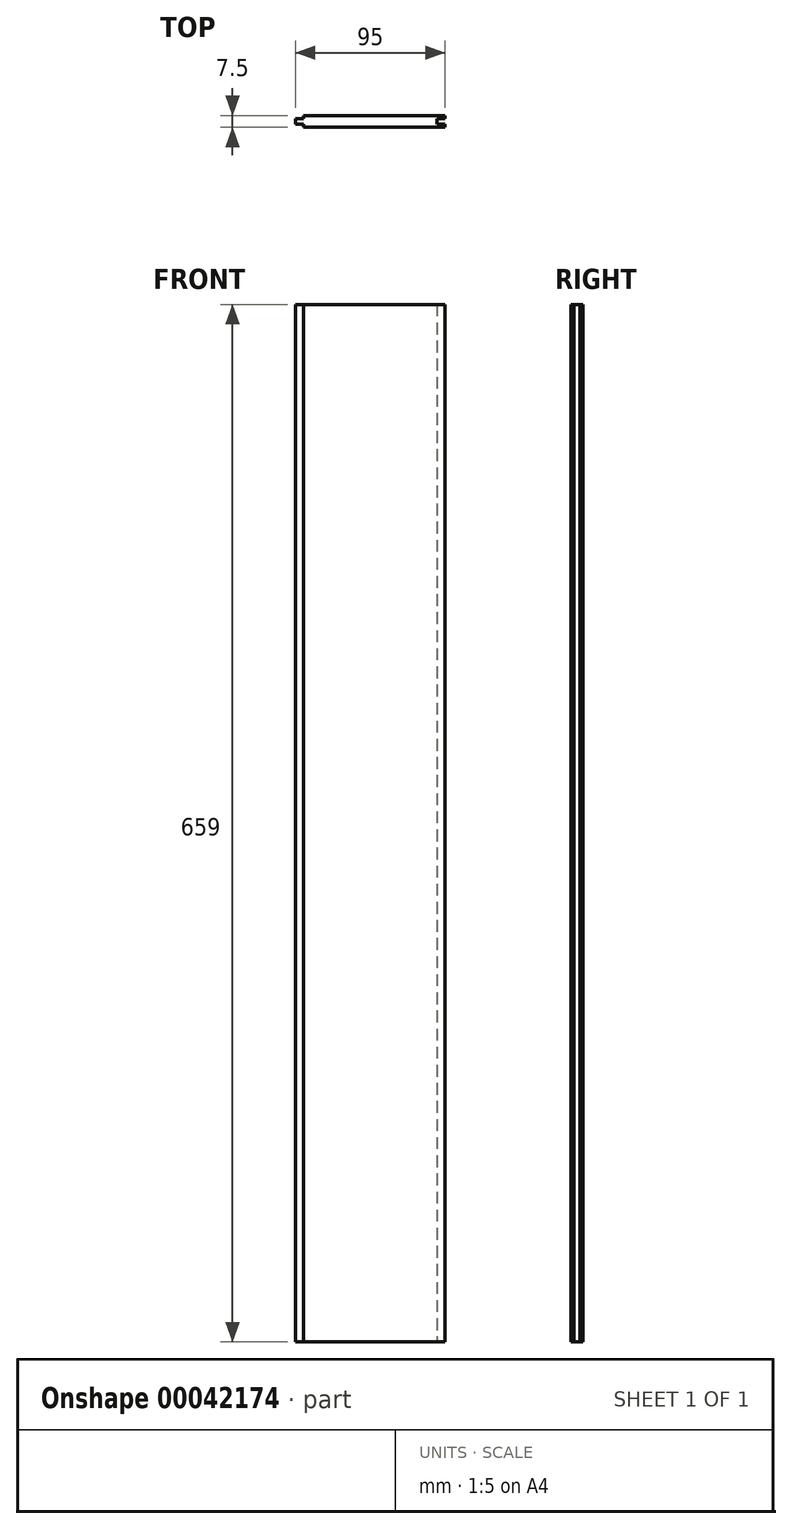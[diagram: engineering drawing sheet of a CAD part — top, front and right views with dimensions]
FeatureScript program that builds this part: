
annotation { "Feature Type Name" : "Feature", "Feature Type Description" : "" }
export const myFeature = defineFeature(function(context is Context, id is Id, definition is map)
    precondition{}
    {
        {
            var Q0;
            Q0=qCreatedBy(makeId("Top.planeOp"),FACE);
            var sketch = newSketch(context, id + "F0", { "sketchPlane" : qUnion([Q0])});
            skLineSegment(sketch, "E0.MirrorCS", {"start": v(-51.23, -6.58) * mm, "end": v(38.77, -6.58) * mm});
            skLineSegment(sketch, "E1", {"start": v(-51.23, 0.92) * mm, "end": v(38.77, 0.92) * mm});
            skLineSegment(sketch, "E2", {"start": v(38.77, -0.96) * mm, "end": v(33.77, -0.96) * mm});
            skLineSegment(sketch, "E3", {"start": v(33.77, -0.96) * mm, "end": v(33.77, -2.83) * mm});
            skLineSegment(sketch, "E4.MirrorCS", {"start": v(38.77, -4.7) * mm, "end": v(33.77, -4.7) * mm});
            skLineSegment(sketch, "E5", {"start": v(-51.23, -0.96) * mm, "end": v(-51.23, 0.92) * mm});
            skLineSegment(sketch, "E6", {"start": v(38.77, 0.92) * mm, "end": v(38.77, -0.96) * mm});
            skLineSegment(sketch, "E7.MirrorCS", {"start": v(-56.23, -4.7) * mm, "end": v(-51.23, -4.7) * mm});
            skLineSegment(sketch, "E8.MirrorCS", {"start": v(-51.23, -4.7) * mm, "end": v(-51.23, -6.58) * mm});
            skLineSegment(sketch, "E9", {"start": v(-56.23, -0.96) * mm, "end": v(-51.23, -0.96) * mm});
            skLineSegment(sketch, "E10", {"start": v(-56.23, -2.83) * mm, "end": v(-56.23, -0.96) * mm});
            skLineSegment(sketch, "E11", {"start": v(33.77, -2.83) * mm, "end": v(33.77, -4.7) * mm});
            skLineSegment(sketch, "E12", {"start": v(38.77, -4.7) * mm, "end": v(38.77, -6.58) * mm});
            skLineSegment(sketch, "E13", {"start": v(-56.23, -4.7) * mm, "end": v(-56.23, -2.83) * mm});
            skSolve(sketch);
        }
        {
            var Q0;
            Q0=makeQuery(id+"F0.imprint","IMPRINT",FACE,{"disambiguationData":[TD([[makeQuery(id+"F0.imprint","IMPRINT",EDGE,{"derivedFrom":sQuery(id+"F0.wireOp",EDGE,"E0.MirrorCS")}),1.0]])]});
            extrude(context, id + "F1", {"entities" : qUnion([Q0]), "depth" : 659 * mm});
        }
    });
